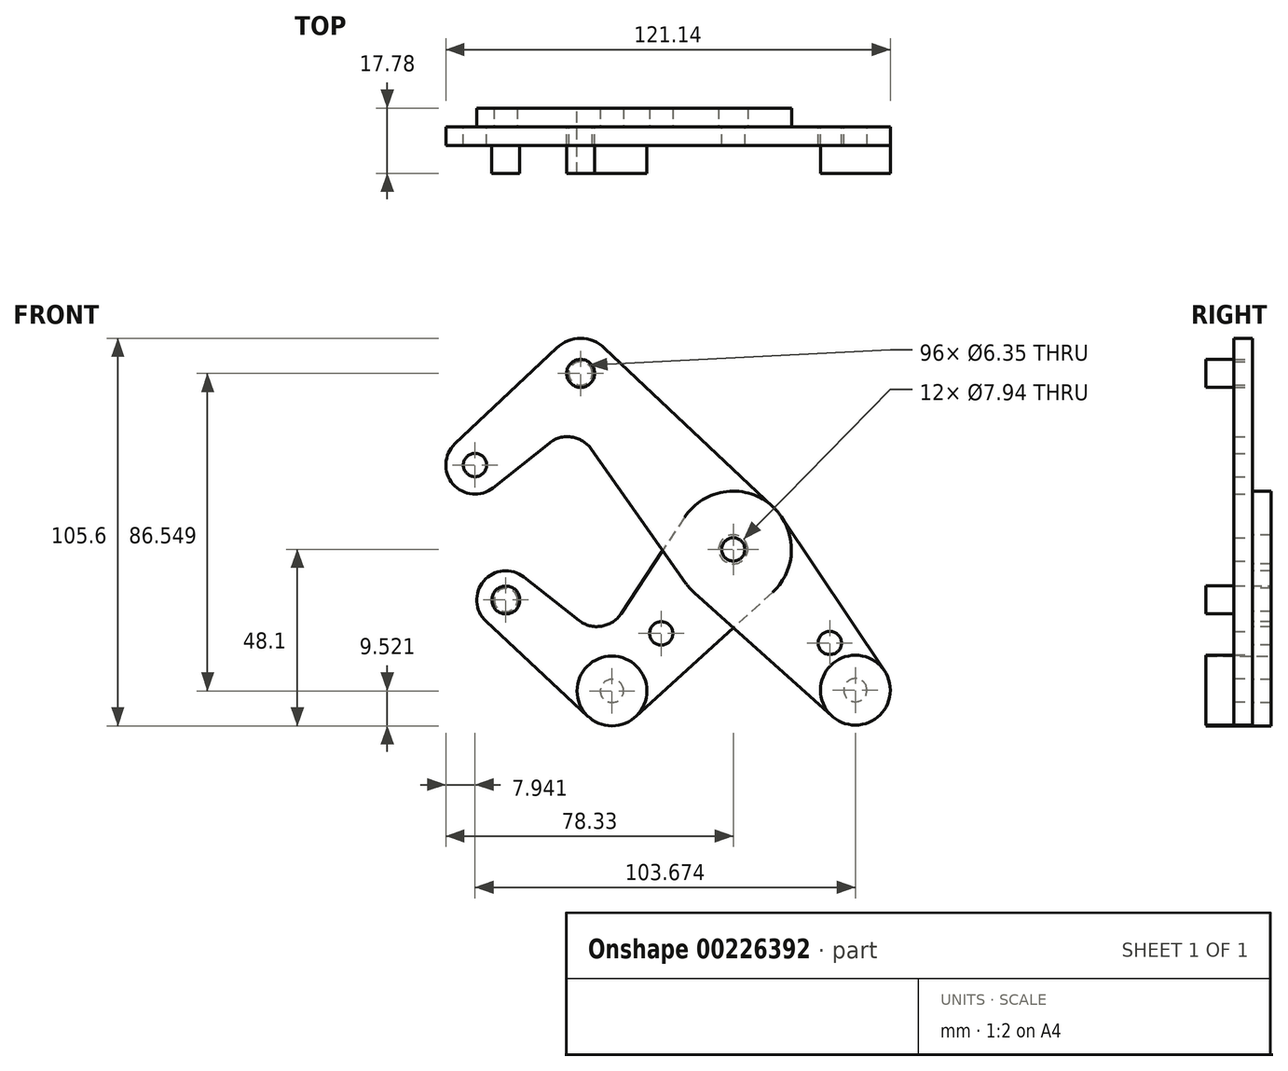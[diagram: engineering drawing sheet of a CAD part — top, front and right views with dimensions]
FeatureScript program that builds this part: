
annotation { "Feature Type Name" : "Feature", "Feature Type Description" : "" }
export const myFeature = defineFeature(function(context is Context, id is Id, definition is map)
    precondition{}
    {
        {
            var Q0;
            Q0=qCreatedBy(makeId("Front.planeOp"),FACE);
            var sketch = newSketch(context, id + "F0", { "sketchPlane" : qUnion([Q0])});
            skLineSegment(sketch, "E0", {"start": v(-41.6, 47.97) * mm, "end": v(41.6, -47.97) * mm, "construction": true});
            skCircle(sketch, "E1", {"center": v(0, 0) * mm, "radius": 3.18 * mm});
            skCircle(sketch, "E2", {"center": v(33.29, -38.38) * mm, "radius": 3.18 * mm});
            skCircle(sketch, "E3", {"center": v(-41.6, 47.97) * mm, "radius": 3.18 * mm});
            skCircle(sketch, "E4", {"center": v(-70.39, 23) * mm, "radius": 3.18 * mm});
            skLineSegment(sketch, "E5", {"start": v(-41.6, 47.97) * mm, "end": v(-70.39, 23) * mm, "construction": true});
            skCircle(sketch, "E6", {"center": v(33.29, -38.38) * mm, "radius": 9.53 * mm});
            skCircle(sketch, "E7", {"center": v(-70.39, 23) * mm, "radius": 7.94 * mm});
            skCircle(sketch, "E8", {"center": v(-41.6, 47.97) * mm, "radius": 9.53 * mm});
            skLineSegment(sketch, "E9", {"start": v(-75.83, 28.78) * mm, "end": v(-48.14, 54.9) * mm});
            skLineSegment(sketch, "E10", {"start": v(-65.44, 16.8) * mm, "end": v(-50.15, 28.98) * mm});
            skCircle(sketch, "E11", {"center": v(0, 0) * mm, "radius": 15.88 * mm});
            skLineSegment(sketch, "E12", {"start": v(-35.07, 54.9) * mm, "end": v(10.9, 11.55) * mm});
            skLineSegment(sketch, "E13", {"start": v(-38.72, 27.35) * mm, "end": v(-12.97, -9.15) * mm});
            skLineSegment(sketch, "E14", {"start": v(-10.6, -11.82) * mm, "end": v(26.93, -45.47) * mm});
            skLineSegment(sketch, "E15", {"start": v(13.2, 8.82) * mm, "end": v(41.2, -33.08) * mm});
            skArc(sketch, "E16.filletArc", {"start": v(-38.72, 27.35) * mm, "mid": v(-44.08, 30.63) * mm, "end": v(-50.15, 28.98) * mm});
            skLineSegment(sketch, "E17", {"start": v(0, 0) * mm, "end": v(-33.05, -38.58) * mm, "construction": true});
            skLineSegment(sketch, "E18", {"start": v(-33.05, -38.58) * mm, "end": v(-61.98, -13.8) * mm, "construction": true});
            skCircle(sketch, "E19", {"center": v(-61.98, -13.8) * mm, "radius": 3.18 * mm});
            skCircle(sketch, "E20", {"center": v(-33.05, -38.58) * mm, "radius": 3.18 * mm});
            skCircle(sketch, "E21", {"center": v(-61.98, -13.8) * mm, "radius": 7.94 * mm});
            skCircle(sketch, "E22", {"center": v(-33.05, -38.58) * mm, "radius": 9.53 * mm});
            skLineSegment(sketch, "E23", {"start": v(-57.08, -7.55) * mm, "end": v(-42.08, -19.35) * mm});
            skLineSegment(sketch, "E24", {"start": v(-67.4, -19.6) * mm, "end": v(-39.54, -45.55) * mm});
            skLineSegment(sketch, "E25", {"start": v(-13.25, 8.74) * mm, "end": v(-30.55, -17.48) * mm});
            skLineSegment(sketch, "E26", {"start": v(10.67, -11.75) * mm, "end": v(-26.65, -45.63) * mm});
            skArc(sketch, "E27.filletArc", {"start": v(-42.08, -19.35) * mm, "mid": v(-35.9, -20.95) * mm, "end": v(-30.55, -17.48) * mm});
            skCircle(sketch, "E28", {"center": v(-19.62, -22.9) * mm, "radius": 3.18 * mm});
            skCircle(sketch, "E29", {"center": v(26.32, -25.5) * mm, "radius": 3.18 * mm});
            skLineSegment(sketch, "E30", {"start": v(26.32, -25.5) * mm, "end": v(23.92, -27.58) * mm, "construction": true});
            skCircle(sketch, "E31", {"center": v(0, 0) * mm, "radius": 3.97 * mm});
            skSolve(sketch);
        }
        {
            var Q0;
            Q0=qCreatedBy(makeId("Front.planeOp"),FACE);
            cPlane(context, id + "F1", {"entities" : qUnion([Q0]), "cplaneType" : CPlaneType.OFFSET, "offset" : 12.7 * mm, "width" : 254 * mm, "height" : 254 * mm});
        }
        {
            var Q0;
            Q0=makeQuery(id+"F0.imprint","IMPRINT",FACE,{"disambiguationData":[TD([[makeQuery(id+"F0.imprint","IMPRINT",EDGE,{"derivedFrom":sQuery(id+"F0.wireOp",EDGE,"E4")}),-1.0]])]});
            var Q1;
            {var subQ1=sQuery(id+"F0.wireOp",EDGE,"E9");Q1=makeQuery(id+"F0.imprint","IMPRINT",FACE,{"disambiguationData":[TD([[makeQuery(id+"F0.imprint","IMPRINT",EDGE,{"derivedFrom":subQ1}),-1.0]])]});}
            var Q2;
            Q2=makeQuery(id+"F0.imprint","IMPRINT",FACE,{"disambiguationData":[TD([[makeQuery(id+"F0.imprint","IMPRINT",EDGE,{"derivedFrom":sQuery(id+"F0.wireOp",EDGE,"E3")}),-1.0]])]});
            var Q3;
            Q3=makeQuery(id+"F0.imprint","IMPRINT",FACE,{"disambiguationData":[TD([[makeQuery(id+"F0.imprint","IMPRINT",EDGE,{"derivedFrom":sQuery(id+"F0.wireOp",EDGE,"E31")}),-1.0]])]});
            var Q4;
            {var subQ0=sQuery(id+"F0.wireOp",EDGE,"E13");var subQ1=sQuery(id+"F0.wireOp",EDGE,"E11");var subQ2=makeQuery(id+"F0.imprint","INTERSECT",VERTEX,{"derivedFrom":[subQ1,subQ0]});Q4=makeQuery(id+"F0.imprint","IMPRINT",FACE,{"disambiguationData":[TD([[makeQuery(id+"F0.imprint","IMPRINT",EDGE,{"disambiguationData":[TD([[subQ2,1.0]])],"derivedFrom":subQ1}),-1.0]])]});}
            var Q5;
            {var subQ0=sQuery(id+"F0.wireOp",EDGE,"E14");var subQ1=sQuery(id+"F0.wireOp",EDGE,"E11");var subQ2=makeQuery(id+"F0.imprint","INTERSECT",VERTEX,{"derivedFrom":[subQ1,subQ0]});Q5=makeQuery(id+"F0.imprint","IMPRINT",FACE,{"disambiguationData":[TD([[makeQuery(id+"F0.imprint","IMPRINT",EDGE,{"disambiguationData":[TD([[subQ2,-1.0]])],"derivedFrom":subQ1}),-1.0]])]});}
            var Q6;
            {var subQ0=sQuery(id+"F0.wireOp",EDGE,"E15");Q6=makeQuery(id+"F0.imprint","IMPRINT",FACE,{"disambiguationData":[TD([[makeQuery(id+"F0.imprint","IMPRINT",EDGE,{"derivedFrom":subQ0}),-1.0]])]});}
            var Q7;
            Q7=makeQuery(id+"F0.imprint","IMPRINT",FACE,{"disambiguationData":[TD([[makeQuery(id+"F0.imprint","IMPRINT",EDGE,{"derivedFrom":sQuery(id+"F0.wireOp",EDGE,"E2")}),-1.0]])]});
            var Q8;
            Q8=makeQuery(id+"F0.imprint","IMPRINT",FACE,{"disambiguationData":[TD([[makeQuery(id+"F0.imprint","IMPRINT",EDGE,{"derivedFrom":sQuery(id+"F0.wireOp",EDGE,"E1")}),-1.0]])]});
            extrude(context, id + "F2", {"entities" : qUnion([Q0, Q1, Q2, Q3, Q4, Q5, Q6, Q7, Q8]), "depth" : 5.08 * mm});
        }
        {
            var Q0;
            Q0=makeQuery(id+"F0.imprint","IMPRINT",FACE,{"disambiguationData":[TD([[makeQuery(id+"F0.imprint","IMPRINT",EDGE,{"derivedFrom":sQuery(id+"F0.wireOp",EDGE,"E31")}),-1.0]])]});
            var Q1;
            {var subQ0=sQuery(id+"F0.wireOp",EDGE,"E14");var subQ1=sQuery(id+"F0.wireOp",EDGE,"E11");var subQ2=makeQuery(id+"F0.imprint","INTERSECT",VERTEX,{"derivedFrom":[subQ1,subQ0]});Q1=makeQuery(id+"F0.imprint","IMPRINT",FACE,{"disambiguationData":[TD([[makeQuery(id+"F0.imprint","IMPRINT",EDGE,{"disambiguationData":[TD([[subQ2,-1.0]])],"derivedFrom":subQ1}),-1.0]])]});}
            var Q2;
            {var subQ10=sQuery(id+"F0.wireOp",EDGE,"E23");Q2=makeQuery(id+"F0.imprint","IMPRINT",FACE,{"disambiguationData":[TD([[makeQuery(id+"F0.imprint","IMPRINT",EDGE,{"derivedFrom":subQ10}),-1.0]])]});}
            var Q3;
            {var subQ0=sQuery(id+"F0.wireOp",EDGE,"E13");var subQ1=sQuery(id+"F0.wireOp",EDGE,"E11");var subQ2=makeQuery(id+"F0.imprint","INTERSECT",VERTEX,{"derivedFrom":[subQ1,subQ0]});Q3=makeQuery(id+"F0.imprint","IMPRINT",FACE,{"disambiguationData":[TD([[makeQuery(id+"F0.imprint","IMPRINT",EDGE,{"disambiguationData":[TD([[subQ2,1.0]])],"derivedFrom":subQ1}),-1.0]])]});}
            var Q4;
            Q4=makeQuery(id+"F0.imprint","IMPRINT",FACE,{"disambiguationData":[TD([[makeQuery(id+"F0.imprint","IMPRINT",EDGE,{"derivedFrom":sQuery(id+"F0.wireOp",EDGE,"E19")}),-1.0]])]});
            var Q5;
            Q5=makeQuery(id+"F0.imprint","IMPRINT",FACE,{"disambiguationData":[TD([[makeQuery(id+"F0.imprint","IMPRINT",EDGE,{"derivedFrom":sQuery(id+"F0.wireOp",EDGE,"E20")}),-1.0]])]});
            extrude(context, id + "F3", {"entities" : qUnion([Q0, Q1, Q2, Q3, Q4, Q5]), "oppositeDirection" : true, "depth" : 5.08 * mm});
        }
        {
            var Q0;
            Q0=makeQuery(id+"F2.opExtrude","CAP_FACE",FACE,{"disambiguationData":[OSD([sQuery(id+"F0.wireOp",EDGE,"E1"),sQuery(id+"F0.wireOp",EDGE,"E2"),sQuery(id+"F0.wireOp",EDGE,"E3"),sQuery(id+"F0.wireOp",EDGE,"E4"),sQuery(id+"F0.wireOp",EDGE,"E6"),sQuery(id+"F0.wireOp",EDGE,"E7"),sQuery(id+"F0.wireOp",EDGE,"E8"),sQuery(id+"F0.wireOp",EDGE,"E9"),sQuery(id+"F0.wireOp",EDGE,"E10"),sQuery(id+"F0.wireOp",EDGE,"E11"),sQuery(id+"F0.wireOp",EDGE,"E12"),sQuery(id+"F0.wireOp",EDGE,"E13"),sQuery(id+"F0.wireOp",EDGE,"E14"),sQuery(id+"F0.wireOp",EDGE,"E15"),sQuery(id+"F0.wireOp",EDGE,"E16.filletArc"),sQuery(id+"F0.wireOp",EDGE,"E29")])],"isStart":true});
            var sketch = newSketch(context, id + "F4", { "sketchPlane" : qUnion([Q0])});
            skCircle(sketch, "E32", {"center": v(41.6, 47.97) * mm, "radius": 3.81 * mm});
            skCircle(sketch, "E33.0", {"center": v(-33.29, -38.38) * mm, "radius": 9.53 * mm});
            skSolve(sketch);
        }
        {
            var Q0;
            Q0=makeQuery(id+"F3.opExtrude","CAP_FACE",FACE,{"disambiguationData":[OSD([sQuery(id+"F0.wireOp",EDGE,"E11"),sQuery(id+"F0.wireOp",EDGE,"E19"),sQuery(id+"F0.wireOp",EDGE,"E20"),sQuery(id+"F0.wireOp",EDGE,"E21"),sQuery(id+"F0.wireOp",EDGE,"E22"),sQuery(id+"F0.wireOp",EDGE,"E23"),sQuery(id+"F0.wireOp",EDGE,"E24"),sQuery(id+"F0.wireOp",EDGE,"E25"),sQuery(id+"F0.wireOp",EDGE,"E26"),sQuery(id+"F0.wireOp",EDGE,"E27.filletArc"),sQuery(id+"F0.wireOp",EDGE,"E28"),sQuery(id+"F0.wireOp",EDGE,"E31")])],"isStart":false});
            var sketch = newSketch(context, id + "F5", { "sketchPlane" : qUnion([Q0])});
            skCircle(sketch, "E34", {"center": v(61.98, -13.8) * mm, "radius": 3.81 * mm});
            skCircle(sketch, "E35.0", {"center": v(33.05, -38.58) * mm, "radius": 9.53 * mm});
            skSolve(sketch);
        }
        {
            var Q0;
            Q0=qSketchRegion(id+"F4",true);
            var Q1;
            Q1=qSketchRegion(id+"F5",true);
            var Q2;
            Q2=qCreatedBy(id+"F1.planeOp",FACE);
            extrude(context, id + "F6", {"entities" : qUnion([Q0, Q1]), "endBound" : BoundingType.UP_TO_SURFACE, "oppositeDirection" : true, "endBoundEntityFace" : qUnion([Q2]), "depth" : 25.4 * mm});
        }
    });
